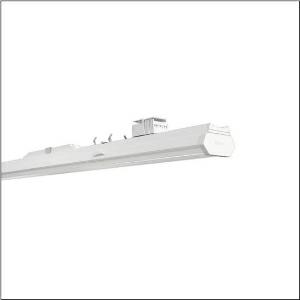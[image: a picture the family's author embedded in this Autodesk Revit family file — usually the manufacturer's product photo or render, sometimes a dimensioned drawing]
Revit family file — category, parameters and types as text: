
# Revit family: licross_r__11_protected_ho_51tp11mn4gxs_ec8e
name_source: partatom
category: Lighting Fixtures
units: mm (PartAtom-declared; Revit-internal decimal feet)

## family parameters
Cut with Voids When Loaded = No
Host = Face
Light Source = No
Part Type = Normal
Room Calculation Point = No
Round Connector Dimension = Use Diameter
Shared = No

## types (1)
- --- (1 x LED, 16070 lm, 87.4 W, 4000K)
    Apparent Load = 87 VA
    CIE Flux Codes = 84 94 98 99 100
    Color Rendering = 80
    Color Temperature = 4000K
    Default Elevation = 1800 mm
    Description = Licross® 11 Protected HO, luminaire insert, of sheet steel, galvanised, coil coated, white, length: 1.500mm, width: 90mm, height: 101mm, LED rated luminous flux: 16.070lm, light colour: 840, control gear: ON/OFF Multilumen, control gear: ECG Multilumen, with plug, 3-pole, with phase selection, mains connection: 220..240V, AC, 50/60Hz, halogen-free wiring, primary light control with lens, of plastic, primary optical cover: cover, of PMMA, light emission: direct with ceiling illumination distribution, primary light characteristic: symmetric, protection rating (complete): IP64, insulation class (complete): insulation class I (protective earthing), certification: CE, ENEC, VDE, UKCA, protection symbol: D if used in an environment with conductive dust loads with corresponding accessories, impact resistance: IK06, permissible ambient temperature for indoor applications: -35..+35°C, corresponds to IFS (International Featured Standards) requirements for safety and quality in the food industry, reducing of maximum allowable ambient temperature of 5°C with ceiling mounting, LABS conformity tested according to VDMA 24364:2018-05, packaging unit: 1 piece
    Height = 92 mm
    Lamp = 1 x LED
    Lamp Light Flux = 16070 lm
    Lamp Power = 87.4 W
    Lamp count = 1
    Length = 1500 mm
    Luminous efficacy = 184 lm/W
    Manufacturer = Siteco
    ModVariant = No
    Model = 51TP11MN4GXS
    Mounting Place = Ceiling
    Mounting Type = Pendant
    Number of Poles = 1
    OnlyDefault = Yes
    Power Factor = 1
    Product Name = Licross® 11 Protected HO
    Product group = luminaire insert
    ProductGroupID = 902
    Protection Class = Protection class I
    Protection Degree = IP 64
    RLX_Detail_Level = 1
    RlxData = <blob elided: 21929 chars, md5=69811bdd>
    Socket = socket
    Standby Power = 0 W
    System Light Flux = 16070 lm
    System Power = 87 W
    Type Comments = factory setting: luminous flux: 100 % | (A | C | E) | 203 mA
    Type Image = l_1256148.jpg
    URL = http://relux.com
    VarID = @adj_003787
    Voltage = 0 V
    Weight = 0.00 kg
    Width = 88 mm

## geometry (parser evidence)
native form markers: Blend x4, Sweep x9
no freeform markers — native parametric forms only
